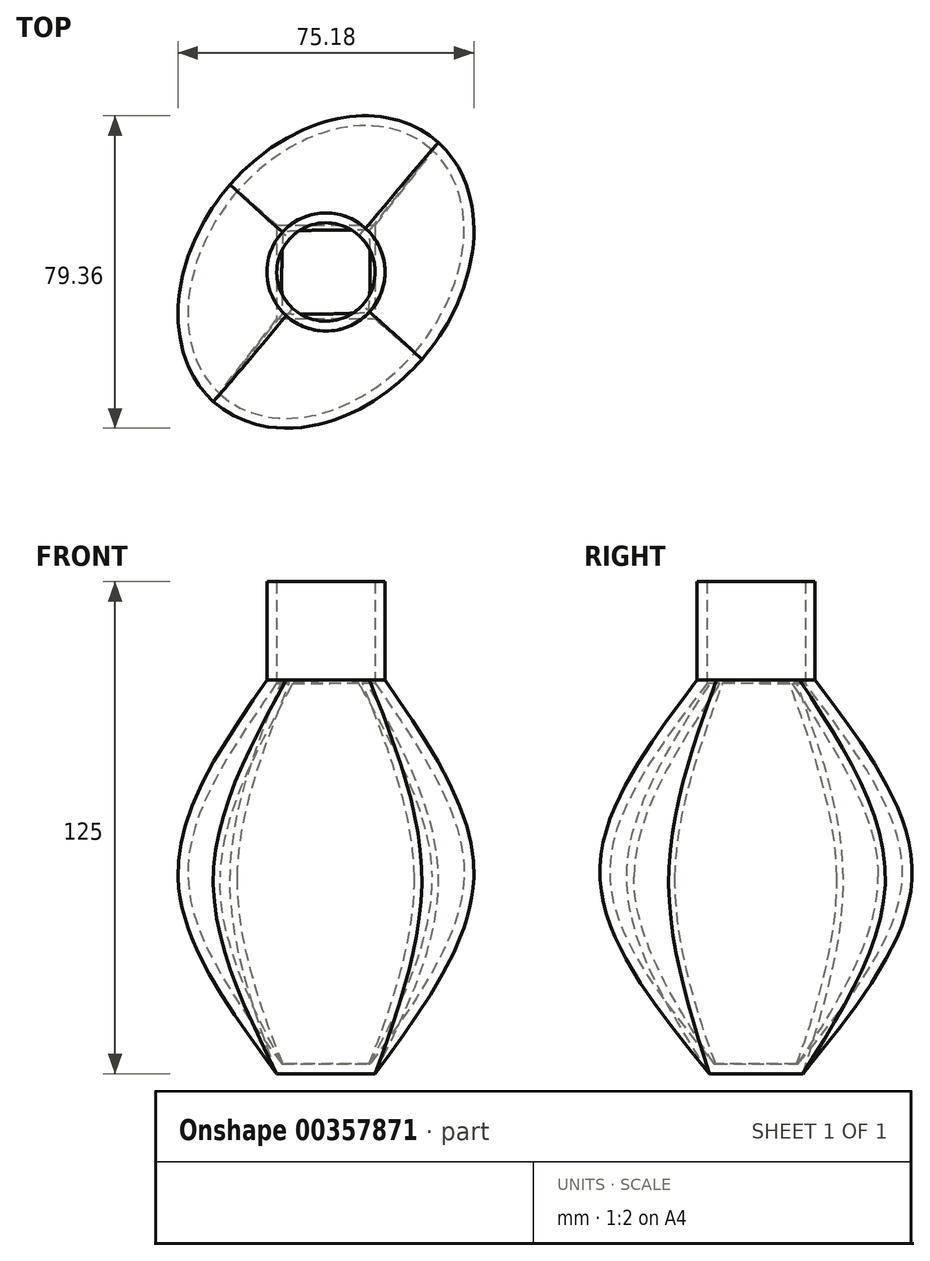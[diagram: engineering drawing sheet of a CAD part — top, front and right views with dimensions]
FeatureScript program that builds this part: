
annotation { "Feature Type Name" : "Feature", "Feature Type Description" : "" }
export const myFeature = defineFeature(function(context is Context, id is Id, definition is map)
    precondition{}
    {
        {
            var Q0;
            Q0=qCreatedBy(makeId("Top.planeOp"),FACE);
            var sketch = newSketch(context, id + "F0", { "sketchPlane" : qUnion([Q0])});
            skLineSegment(sketch, "E0.bottom", {"start": v(-12.5, 11.87) * mm, "end": v(12.5, 11.87) * mm});
            skLineSegment(sketch, "E0.top", {"start": v(-12.5, -11.87) * mm, "end": v(12.5, -11.87) * mm});
            skLineSegment(sketch, "E0.left", {"start": v(-12.5, 11.87) * mm, "end": v(-12.5, -11.87) * mm});
            skLineSegment(sketch, "E0.right", {"start": v(12.5, 11.87) * mm, "end": v(12.5, -11.87) * mm});
            skPoint(sketch, "E0.middle", {"position": v(0, 0) * mm});
            skSolve(sketch);
        }
        {
            var Q0;
            Q0=qCreatedBy(makeId("Top.planeOp"),FACE);
            cPlane(context, id + "F1", {"entities" : qUnion([Q0]), "cplaneType" : CPlaneType.OFFSET, "offset" : 50 * mm, "width" : 152.4 * mm, "height" : 152.4 * mm});
        }
        {
            var Q0;
            Q0=qCreatedBy(id+"F1.planeOp",FACE);
            var sketch = newSketch(context, id + "F2", { "sketchPlane" : qUnion([Q0])});
            skEllipse(sketch, "E1", {"center": v(0, 0) * mm, "majorRadius": 32.93 * mm, "minorRadius": 43.6 * mm, "majorAxis": v(-0.77, 0.63)});
            skSolve(sketch);
        }
        {
            var Q0;
            Q0=qCreatedBy(makeId("Top.planeOp"),FACE);
            cPlane(context, id + "F3", {"entities" : qUnion([Q0]), "cplaneType" : CPlaneType.OFFSET, "offset" : 100 * mm, "width" : 152.4 * mm, "height" : 152.4 * mm});
        }
        {
            var Q0;
            Q0=qCreatedBy(id+"F3.planeOp",FACE);
            var sketch = newSketch(context, id + "F4", { "sketchPlane" : qUnion([Q0])});
            skCircle(sketch, "E2", {"center": v(0, 0) * mm, "radius": 15 * mm});
            skSolve(sketch);
        }
        {
            var Q0;
            Q0=makeQuery(id+"F0.imprint","IMPRINT",FACE,{"disambiguationData":[TD([[makeQuery(id+"F0.imprint","IMPRINT",EDGE,{"derivedFrom":sQuery(id+"F0.wireOp",EDGE,"E0.bottom")}),-1.0]])]});
            var Q1;
            Q1=makeQuery(id+"F2.imprint","IMPRINT",FACE,{"disambiguationData":[TD([[makeQuery(id+"F2.imprint","IMPRINT",EDGE,{"derivedFrom":sQuery(id+"F2.wireOp",EDGE,"E1")}),1.0]])]});
            var Q2;
            Q2=makeQuery(id+"F4.imprint","IMPRINT",FACE,{"disambiguationData":[TD([[makeQuery(id+"F4.imprint","IMPRINT",EDGE,{"derivedFrom":sQuery(id+"F4.wireOp",EDGE,"E2")}),1.0]])]});
            loft(context, id + "F5", {"sheetProfilesArray" : [{ "sheetProfileEntities" : qUnion([Q0]) }, { "sheetProfileEntities" : qUnion([Q1]) }, { "sheetProfileEntities" : qUnion([Q2]) }]});
        }
        {
            var Q0;
            Q0=makeQuery(id+"F5.opLoft","CAP_FACE",FACE,{"disambiguationData":[OSD([makeQuery(id+"F4.imprint","IMPRINT",FACE,{"disambiguationData":[TD([[makeQuery(id+"F4.imprint","IMPRINT",EDGE,{"derivedFrom":sQuery(id+"F4.wireOp",EDGE,"E2")}),1.0]])]})])],"isStart":true});
            extrude(context, id + "F6", {"entities" : qUnion([Q0]), "operationType" : NewBodyOperationType.ADD, "depth" : 10 * mm});
        }
        {
            var Q0;
            Q0=makeQuery(id+"F6.opExtrude","CAP_FACE",FACE,{"disambiguationData":[OSD([makeQuery(id+"F4.imprint","IMPRINT",FACE,{"disambiguationData":[TD([[makeQuery(id+"F4.imprint","IMPRINT",EDGE,{"derivedFrom":sQuery(id+"F4.wireOp",EDGE,"E2")}),1.0]])]})])],"isStart":false});
            extrude(context, id + "F7", {"entities" : qUnion([Q0]), "operationType" : NewBodyOperationType.ADD, "depth" : 15 * mm});
        }
        {
            var Q0;
            Q0=makeQuery(id+"F7.opExtrude","CAP_FACE",FACE,{"disambiguationData":[OSD([makeQuery(id+"F4.imprint","IMPRINT",FACE,{"disambiguationData":[TD([[makeQuery(id+"F4.imprint","IMPRINT",EDGE,{"derivedFrom":sQuery(id+"F4.wireOp",EDGE,"E2")}),1.0]])]})])],"isStart":false});
            shell(context, id + "F8", {"entities" : qUnion([Q0]), "thickness" : 2.5 * mm});
        }
    });
